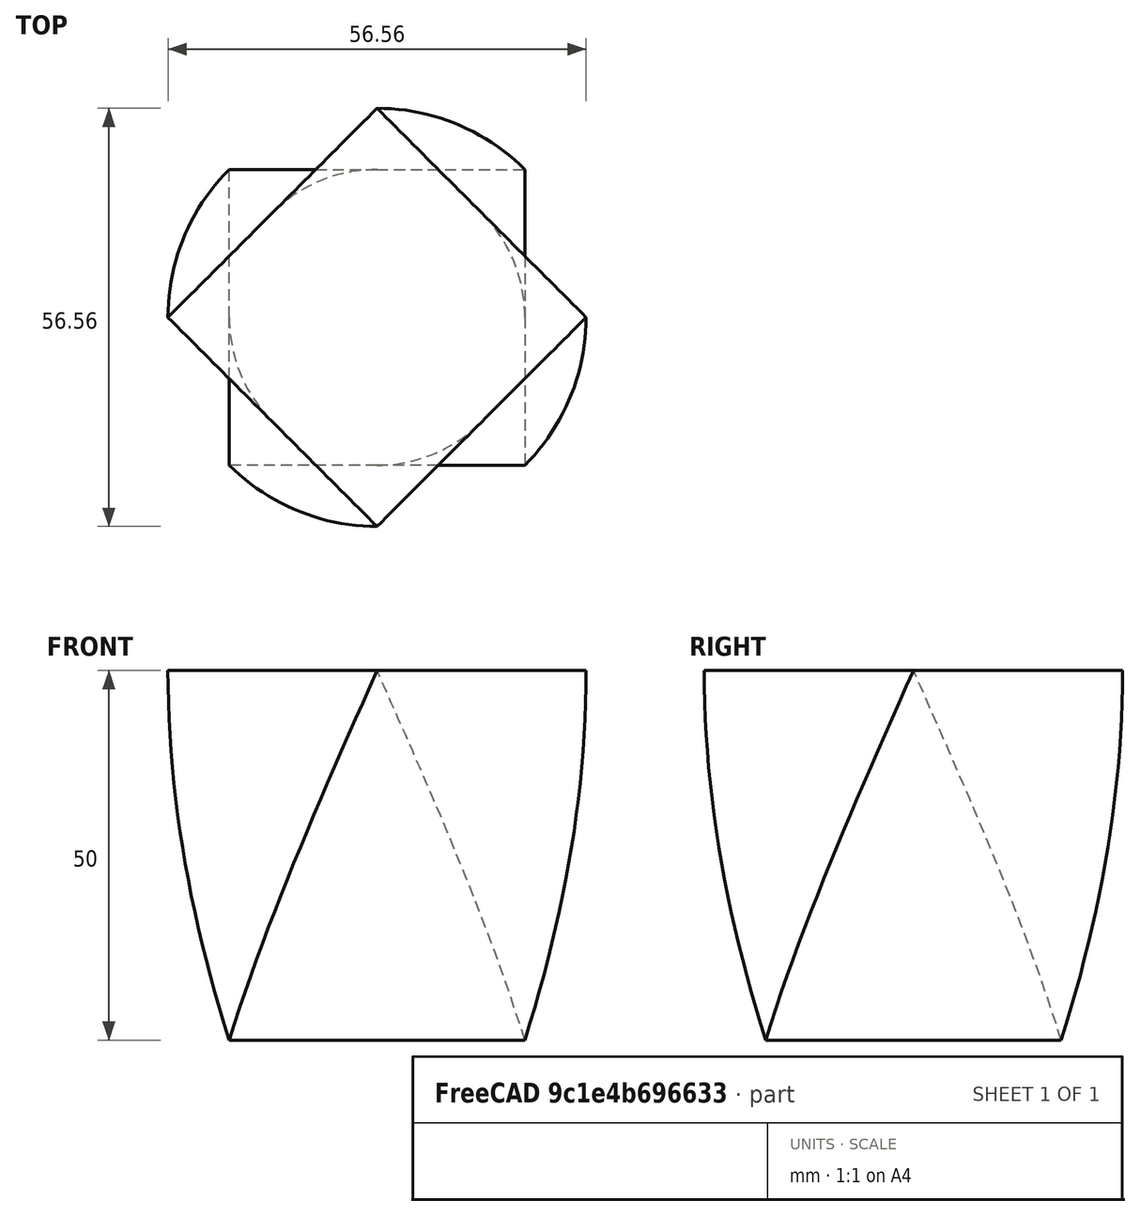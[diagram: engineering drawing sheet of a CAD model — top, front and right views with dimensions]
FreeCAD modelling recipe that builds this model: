
FCSTD DOCUMENT  (FreeCAD 0.16R6707 (Git))
Label: caja-torsion
License: All rights reserved
LicenseURL: http://en.wikipedia.org/wiki/All_rights_reserved
objects: Sketcher::SketchObject×1, Part::Helix×1, Part::Sweep×1
note: 3 computed .brp shape members not serialized (recipe doc carries the construction recipe); baked Part::Feature solids carry a one-line shape summary decoded from their .brp

FEATURE [Sketcher::SketchObject] Sketch
  sketch-geometry (4):
    g0: LineSegment StartX=-20 StartY=20 StartZ=0 EndX=20 EndY=20 EndZ=0
    g1: LineSegment StartX=20 StartY=20 StartZ=0 EndX=20 EndY=-20 EndZ=0
    g2: LineSegment StartX=20 StartY=-20 StartZ=0 EndX=-20 EndY=-20 EndZ=0
    g3: LineSegment StartX=-20 StartY=-20 StartZ=0 EndX=-20 EndY=20 EndZ=0
  constraints (11):
    c: Coincident(g0,g1)
    c: Coincident(g1,g2)
    c: Coincident(g2,g3)
    c: Coincident(g3,g0)
    c: Horizontal(g0)
    c: Horizontal(g2)
    c: Vertical(g1)
    c: Vertical(g3)
    c: Symmetric(g0,g1,g-1)
    c: Equal(g0,g1)
    c: DistanceX(g0,g0) = 40
FEATURE [Part::Helix] Helix  label="Espiral"
  Angle = 0
  Height = 50
  LocalCoord = 0
  Pitch = 400
  Radius = 20
  Style = 1
  expr: Pitch = 360 * 50 / 45
FEATURE [Part::Sweep] Sweep
  Frenet = true
  Sections = -> [Sketch]
  Solid = true
  Spine = -> Helix [Edge1]
  Transition = 1
